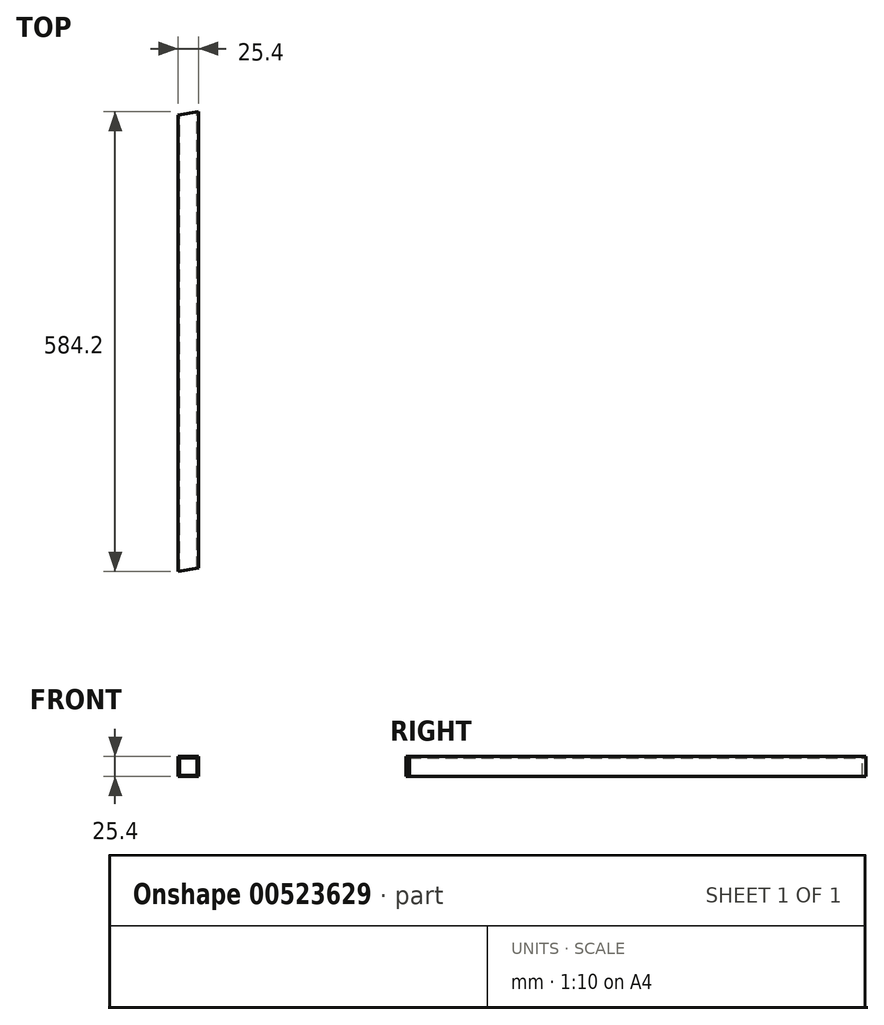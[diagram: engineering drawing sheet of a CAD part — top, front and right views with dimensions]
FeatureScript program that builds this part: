
annotation { "Feature Type Name" : "Feature", "Feature Type Description" : "" }
export const myFeature = defineFeature(function(context is Context, id is Id, definition is map)
    precondition{}
    {
        {
            var Q0;
            Q0=qCreatedBy(makeId("Front.planeOp"),FACE);
            var sketch = newSketch(context, id + "F0", { "sketchPlane" : qUnion([Q0])});
            skLineSegment(sketch, "E0.bottom", {"start": v(-12.7, -12.7) * mm, "end": v(12.7, -12.7) * mm});
            skLineSegment(sketch, "E0.top", {"start": v(-12.7, 12.7) * mm, "end": v(12.7, 12.7) * mm});
            skLineSegment(sketch, "E0.left", {"start": v(-12.7, -12.7) * mm, "end": v(-12.7, 12.7) * mm});
            skLineSegment(sketch, "E0.right", {"start": v(12.7, -12.7) * mm, "end": v(12.7, 12.7) * mm});
            skLineSegment(sketch, "E1.bottom", {"start": v(-11.11, -11.11) * mm, "end": v(11.11, -11.11) * mm});
            skLineSegment(sketch, "E1.top", {"start": v(-11.11, 11.11) * mm, "end": v(11.11, 11.11) * mm});
            skLineSegment(sketch, "E1.left", {"start": v(-11.11, -11.11) * mm, "end": v(-11.11, 11.11) * mm});
            skLineSegment(sketch, "E1.right", {"start": v(11.11, -11.11) * mm, "end": v(11.11, 11.11) * mm});
            skLineSegment(sketch, "E2", {"start": v(-11.11, 0) * mm, "end": v(11.11, 0) * mm, "construction": true});
            skLineSegment(sketch, "E3", {"start": v(0, 12.7) * mm, "end": v(0, -12.7) * mm, "construction": true});
            skSolve(sketch);
        }
        {
            var Q0;
            Q0=qSketchRegion(id+"F0",true);
            extrude(context, id + "F1", {"entities" : qUnion([Q0]), "endBound" : BoundingType.SYMMETRIC, "depth" : 584.2 * mm, "offsetDistance" : 25.4 * mm});
        }
        {
            var Q0;
            Q0=makeQuery(id+"F1.opExtrude","SWEPT_FACE",FACE,{"disambiguationData":[OSD([sQuery(id+"F0.wireOp",EDGE,"E0.top")])]});
            var sketch = newSketch(context, id + "F2", { "sketchPlane" : qUnion([Q0])});
            skLineSegment(sketch, "E4", {"start": v(-12.7, 292.1) * mm, "end": v(-12.7, 287.62) * mm});
            skLineSegment(sketch, "E5", {"start": v(-12.7, 287.62) * mm, "end": v(12.7, 292.1) * mm});
            skLineSegment(sketch, "E6", {"start": v(12.7, 292.1) * mm, "end": v(-12.7, 292.1) * mm});
            skSolve(sketch);
        }
        {
            var Q0;
            Q0=qSketchRegion(id+"F2",true);
            extrude(context, id + "F3", {"entities" : qUnion([Q0]), "operationType" : NewBodyOperationType.REMOVE, "endBound" : BoundingType.THROUGH_ALL, "oppositeDirection" : true, "depth" : 25.4 * mm, "offsetDistance" : 25.4 * mm});
        }
        {
            var Q0;
            Q0=makeQuery(id+"F1.opExtrude","SWEPT_FACE",FACE,{"disambiguationData":[OSD([sQuery(id+"F0.wireOp",EDGE,"E0.top")])]});
            var sketch = newSketch(context, id + "F4", { "sketchPlane" : qUnion([Q0])});
            skLineSegment(sketch, "E7", {"start": v(-12.7, -292.1) * mm, "end": v(12.7, -287.62) * mm});
            skLineSegment(sketch, "E8", {"start": v(12.7, -287.62) * mm, "end": v(12.7, -292.1) * mm});
            skLineSegment(sketch, "E9", {"start": v(12.7, -292.1) * mm, "end": v(-12.7, -292.1) * mm});
            skSolve(sketch);
        }
        {
            var Q0;
            Q0 = qSketchRegion(id + "F4", true);
            extrude(context, id + "F5", {"entities" : qUnion([Q0]), "operationType" : NewBodyOperationType.REMOVE, "endBound" : BoundingType.THROUGH_ALL, "oppositeDirection" : true, "depth" : 25.4 * mm, "offsetDistance" : 25.4 * mm});
        }
    });
